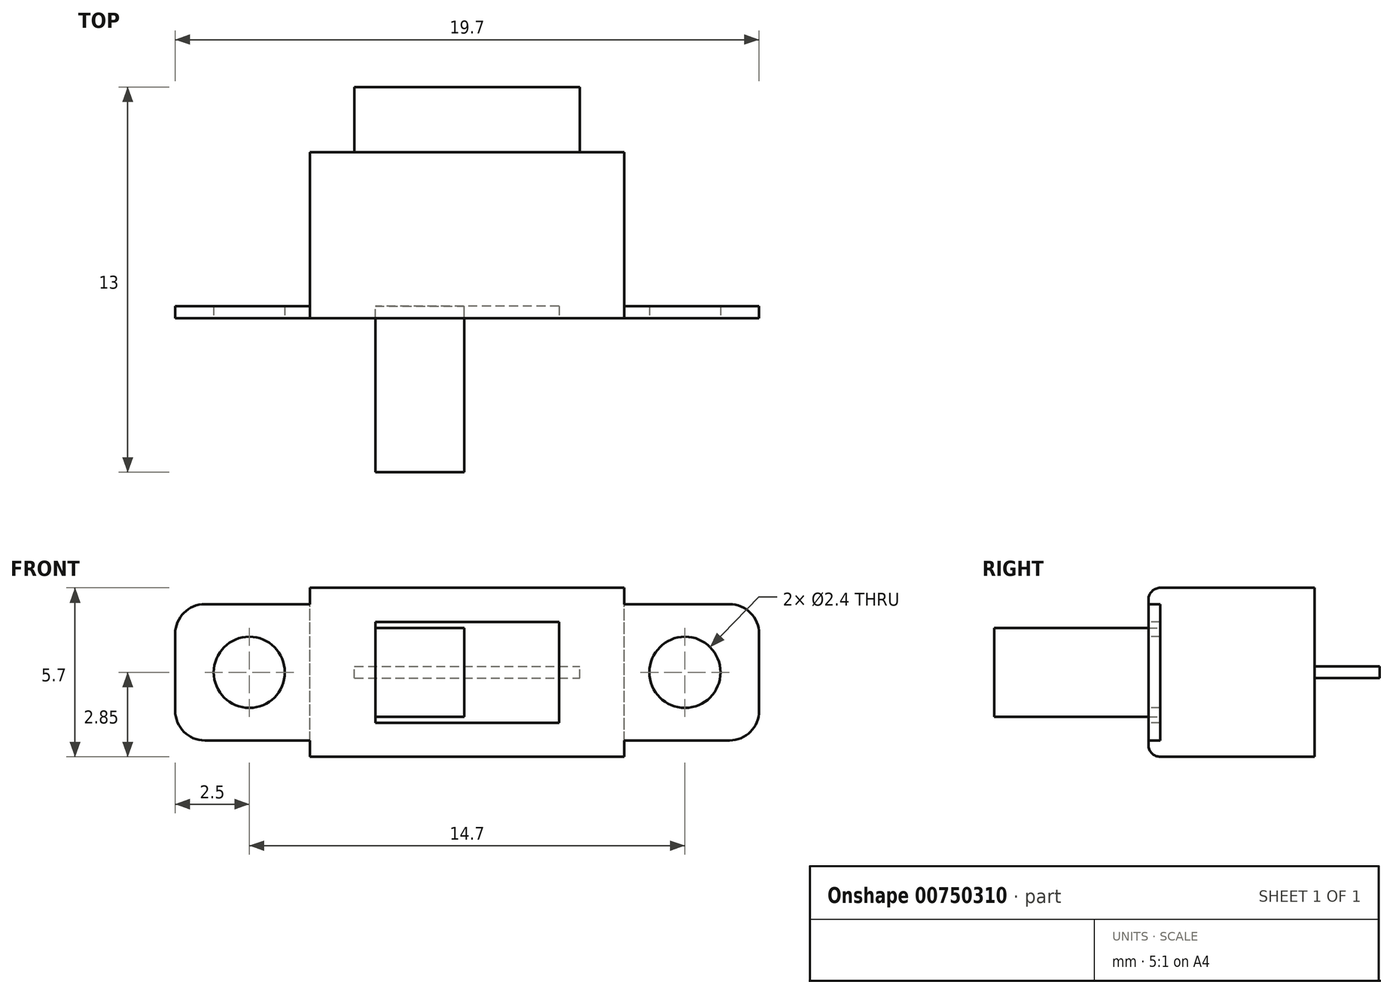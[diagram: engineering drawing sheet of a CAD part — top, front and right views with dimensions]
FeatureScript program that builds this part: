
annotation { "Feature Type Name" : "Feature", "Feature Type Description" : "" }
export const myFeature = defineFeature(function(context is Context, id is Id, definition is map)
    precondition{}
    {
        {
            var Q0;
            Q0=qCreatedBy(makeId("Front.planeOp"),FACE);
            var sketch = newSketch(context, id + "F0", { "sketchPlane" : qUnion([Q0])});
            skLineSegment(sketch, "E0.bottom", {"start": v(9.85, -2.3) * mm, "end": v(-9.85, -2.3) * mm});
            skLineSegment(sketch, "E0.top", {"start": v(9.85, 2.3) * mm, "end": v(-9.85, 2.3) * mm});
            skLineSegment(sketch, "E0.left", {"start": v(9.85, -2.3) * mm, "end": v(9.85, 2.3) * mm});
            skLineSegment(sketch, "E0.right", {"start": v(-9.85, -2.3) * mm, "end": v(-9.85, 2.3) * mm});
            skPoint(sketch, "E0.middle", {"position": v(0, 0) * mm});
            skLineSegment(sketch, "E1.bottom", {"start": v(5.3, -2.85) * mm, "end": v(-5.3, -2.85) * mm});
            skLineSegment(sketch, "E1.top", {"start": v(5.3, 2.85) * mm, "end": v(-5.3, 2.85) * mm});
            skLineSegment(sketch, "E1.left", {"start": v(5.3, -2.85) * mm, "end": v(5.3, 2.85) * mm});
            skLineSegment(sketch, "E1.right", {"start": v(-5.3, -2.85) * mm, "end": v(-5.3, 2.85) * mm});
            skSolve(sketch);
        }
        {
            var Q0;
            Q0 = qSketchRegion(id + "F0", true);
            extrude(context, id + "F1", {"entities" : qUnion([Q0]), "depth" : .4 * mm, "offsetDistance" : 25 * mm});
        }
        {
            var Q0;
            Q0=makeQuery(id+"F1.opExtrude","CAP_FACE",FACE,{"disambiguationData":[OSD([sQuery(id+"F0.wireOp",EDGE,"E0.bottom"),sQuery(id+"F0.wireOp",EDGE,"E0.top"),sQuery(id+"F0.wireOp",EDGE,"E0.left"),sQuery(id+"F0.wireOp",EDGE,"E0.right"),sQuery(id+"F0.wireOp",EDGE,"E1.bottom"),sQuery(id+"F0.wireOp",EDGE,"E1.top"),sQuery(id+"F0.wireOp",EDGE,"E1.left"),sQuery(id+"F0.wireOp",EDGE,"E1.right")])],"isStart":false});
            var sketch = newSketch(context, id + "F2", { "sketchPlane" : qUnion([Q0])});
            skCircle(sketch, "E2", {"center": v(-7.35, 0) * mm, "radius": 1.2 * mm});
            skCircle(sketch, "E3", {"center": v(7.35, 0) * mm, "radius": 1.2 * mm});
            skSolve(sketch);
        }
        {
            var Q0;
            Q0 = qSketchRegion(id + "F2", true);
            extrude(context, id + "F3", {"entities" : qUnion([Q0]), "operationType" : NewBodyOperationType.REMOVE, "oppositeDirection" : true, "depth" : .5 * mm, "offsetDistance" : 25 * mm});
        }
        {
            var Q0;
            Q0=makeQuery(id+"F1.opExtrude","CAP_EDGE",EDGE,{"disambiguationData":[OSD([sQuery(id+"F0.wireOp",EDGE,"E1.top")])],"isStart":false});
            var Q1;
            Q1=makeQuery(id+"F1.opExtrude","CAP_EDGE",EDGE,{"disambiguationData":[OSD([sQuery(id+"F0.wireOp",EDGE,"E1.bottom")])],"isStart":false});
            fillet(context, id + "F4", {"entities" : qUnion([Q0, Q1]), "radius" : .4 * mm, "tangentPropagation" : true, "allowEdgeOverflow" : false});
        }
        {
            var Q0;
            Q0=makeQuery(id+"F1.opExtrude","CAP_FACE",FACE,{"disambiguationData":[OSD([sQuery(id+"F0.wireOp",EDGE,"E0.bottom"),sQuery(id+"F0.wireOp",EDGE,"E0.top"),sQuery(id+"F0.wireOp",EDGE,"E0.left"),sQuery(id+"F0.wireOp",EDGE,"E0.right"),sQuery(id+"F0.wireOp",EDGE,"E1.bottom"),sQuery(id+"F0.wireOp",EDGE,"E1.top"),sQuery(id+"F0.wireOp",EDGE,"E1.left"),sQuery(id+"F0.wireOp",EDGE,"E1.right")])],"isStart":true});
            var sketch = newSketch(context, id + "F5", { "sketchPlane" : qUnion([Q0])});
            skLineSegment(sketch, "E4.bottom", {"start": v(-5.3, 2.85) * mm, "end": v(5.3, 2.85) * mm});
            skLineSegment(sketch, "E4.top", {"start": v(-5.3, -2.85) * mm, "end": v(5.3, -2.85) * mm});
            skLineSegment(sketch, "E4.left", {"start": v(-5.3, 2.85) * mm, "end": v(-5.3, -2.85) * mm});
            skLineSegment(sketch, "E4.right", {"start": v(5.3, 2.85) * mm, "end": v(5.3, -2.85) * mm});
            skSolve(sketch);
        }
        {
            var Q0;
            Q0 = qSketchRegion(id + "F5", true);
            extrude(context, id + "F6", {"entities" : qUnion([Q0]), "operationType" : NewBodyOperationType.ADD, "depth" : 5.2 * mm, "offsetDistance" : 25 * mm});
        }
        {
            var Q0;
            Q0=makeQuery(id+"F1.opExtrude","SWEPT_EDGE",EDGE,{"disambiguationData":[OSD([sQuery(id+"F0.wireOp",EDGE,"E0.top"),sQuery(id+"F0.wireOp",EDGE,"E0.left")])]});
            var Q1;
            Q1=makeQuery(id+"F1.opExtrude","SWEPT_EDGE",EDGE,{"disambiguationData":[OSD([sQuery(id+"F0.wireOp",EDGE,"E0.bottom"),sQuery(id+"F0.wireOp",EDGE,"E0.left")])]});
            var Q2;
            Q2=makeQuery(id+"F1.opExtrude","SWEPT_EDGE",EDGE,{"disambiguationData":[OSD([sQuery(id+"F0.wireOp",EDGE,"E0.bottom"),sQuery(id+"F0.wireOp",EDGE,"E0.right")])]});
            var Q3;
            Q3=makeQuery(id+"F1.opExtrude","SWEPT_EDGE",EDGE,{"disambiguationData":[OSD([sQuery(id+"F0.wireOp",EDGE,"E0.top"),sQuery(id+"F0.wireOp",EDGE,"E0.right")])]});
            fillet(context, id + "F7", {"entities" : qUnion([Q0, Q1, Q2, Q3]), "radius" : 1 * mm, "tangentPropagation" : true, "allowEdgeOverflow" : false});
        }
        {
            var Q0;
            Q0=makeQuery(id+"F1.opExtrude","CAP_FACE",FACE,{"disambiguationData":[OSD([sQuery(id+"F0.wireOp",EDGE,"E0.bottom"),sQuery(id+"F0.wireOp",EDGE,"E0.top"),sQuery(id+"F0.wireOp",EDGE,"E0.left"),sQuery(id+"F0.wireOp",EDGE,"E0.right"),sQuery(id+"F0.wireOp",EDGE,"E1.bottom"),sQuery(id+"F0.wireOp",EDGE,"E1.top"),sQuery(id+"F0.wireOp",EDGE,"E1.left"),sQuery(id+"F0.wireOp",EDGE,"E1.right")])],"isStart":false});
            var sketch = newSketch(context, id + "F8", { "sketchPlane" : qUnion([Q0])});
            skLineSegment(sketch, "E5.bottom", {"start": v(3.1, -1.7) * mm, "end": v(-3.1, -1.7) * mm});
            skLineSegment(sketch, "E5.top", {"start": v(3.1, 1.7) * mm, "end": v(-3.1, 1.7) * mm});
            skLineSegment(sketch, "E5.left", {"start": v(3.1, -1.7) * mm, "end": v(3.1, 1.7) * mm});
            skLineSegment(sketch, "E5.right", {"start": v(-3.1, -1.7) * mm, "end": v(-3.1, 1.7) * mm});
            skPoint(sketch, "E5.middle", {"position": v(0, 0) * mm});
            skSolve(sketch);
        }
        {
            var Q0;
            Q0 = qSketchRegion(id + "F8", true);
            extrude(context, id + "F9", {"entities" : qUnion([Q0]), "operationType" : NewBodyOperationType.REMOVE, "oppositeDirection" : true, "depth" : .4 * mm, "offsetDistance" : 25 * mm});
        }
        {
            var Q0;
            Q0=makeQuery(id+"F9.boolean.opBoolean","COPY",FACE,{"derivedFrom":makeQuery(id+"F9.opExtrude","CAP_FACE",FACE,{"disambiguationData":[OSD([sQuery(id+"F8.wireOp",EDGE,"E5.bottom"),sQuery(id+"F8.wireOp",EDGE,"E5.top"),sQuery(id+"F8.wireOp",EDGE,"E5.left"),sQuery(id+"F8.wireOp",EDGE,"E5.right")])],"isStart":false})});
            var sketch = newSketch(context, id + "F10", { "sketchPlane" : qUnion([Q0])});
            skLineSegment(sketch, "E6.bottom", {"start": v(-3.1, 1.5) * mm, "end": v(-0.1, 1.5) * mm});
            skLineSegment(sketch, "E6.top", {"start": v(-3.1, -1.5) * mm, "end": v(-0.1, -1.5) * mm});
            skLineSegment(sketch, "E6.left", {"start": v(-3.1, 1.5) * mm, "end": v(-3.1, -1.5) * mm});
            skLineSegment(sketch, "E6.right", {"start": v(-0.1, 1.5) * mm, "end": v(-0.1, -1.5) * mm});
            skSolve(sketch);
        }
        {
            var Q0;
            Q0 = qSketchRegion(id + "F10", true);
            extrude(context, id + "F11", {"entities" : qUnion([Q0]), "operationType" : NewBodyOperationType.ADD, "depth" : 5.6 * mm, "offsetDistance" : 25 * mm});
        }
        {
            var Q0;
            Q0=makeQuery(id+"F6.opExtrude","CAP_FACE",FACE,{"disambiguationData":[OSD([sQuery(id+"F5.wireOp",EDGE,"E4.bottom"),sQuery(id+"F5.wireOp",EDGE,"E4.top"),sQuery(id+"F5.wireOp",EDGE,"E4.left"),sQuery(id+"F5.wireOp",EDGE,"E4.right")])],"isStart":false});
            var sketch = newSketch(context, id + "F12", { "sketchPlane" : qUnion([Q0])});
            skLineSegment(sketch, "E7.bottom", {"start": v(3.8, -0.2) * mm, "end": v(-3.8, -0.2) * mm});
            skLineSegment(sketch, "E7.top", {"start": v(3.8, 0.2) * mm, "end": v(-3.8, 0.2) * mm});
            skLineSegment(sketch, "E7.left", {"start": v(3.8, -0.2) * mm, "end": v(3.8, 0.2) * mm});
            skLineSegment(sketch, "E7.right", {"start": v(-3.8, -0.2) * mm, "end": v(-3.8, 0.2) * mm});
            skPoint(sketch, "E7.middle", {"position": v(0, 0) * mm});
            skSolve(sketch);
        }
        {
            var Q0;
            Q0 = qSketchRegion(id + "F12", true);
            extrude(context, id + "F13", {"entities" : qUnion([Q0]), "operationType" : NewBodyOperationType.ADD, "depth" : 2.2 * mm, "offsetDistance" : 25 * mm});
        }
    });
